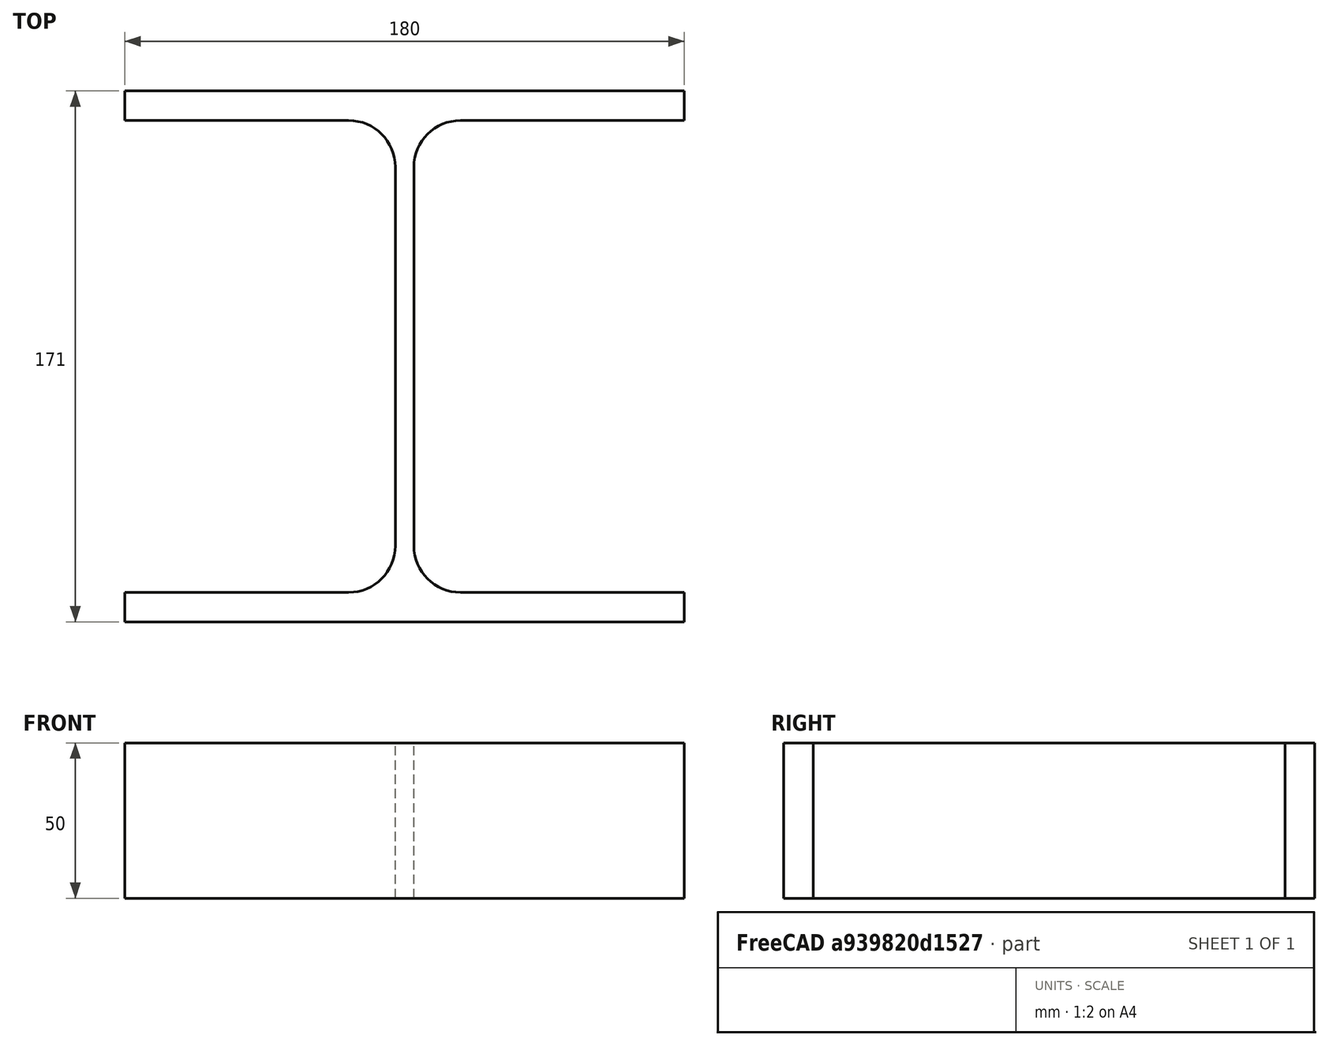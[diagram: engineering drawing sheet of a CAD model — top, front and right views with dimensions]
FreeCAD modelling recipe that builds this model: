
FCSTD DOCUMENT  (FreeCAD 0.15R4671 (Git))
Label: HE-A-Profile 180 DIN1025-3 S235JR
License: All rights reserved
LicenseURL: http://en.wikipedia.org/wiki/All_rights_reserved
objects: Sketcher::SketchObject×1, Part::Extrusion×1
note: 2 computed .brp shape members not serialized (recipe doc carries the construction recipe); baked Part::Feature solids carry a one-line shape summary decoded from their .brp

FEATURE [Sketcher::SketchObject] Sketch
  sketch-geometry (16):
    g0: LineSegment StartX=3 StartY=-61 StartZ=0 EndX=3 EndY=61 EndZ=0
    g1: LineSegment StartX=18 StartY=76 StartZ=0 EndX=90 EndY=76 EndZ=0
    g2: LineSegment StartX=90 StartY=76 StartZ=0 EndX=90 EndY=85.5 EndZ=0
    g3: LineSegment StartX=90 StartY=85.5 StartZ=0 EndX=-90 EndY=85.5 EndZ=0
    g4: LineSegment StartX=-90 StartY=85.5 StartZ=0 EndX=-90 EndY=76 EndZ=0
    g5: LineSegment StartX=-90 StartY=76 StartZ=0 EndX=-18 EndY=76 EndZ=0
    g6: LineSegment StartX=-3 StartY=61 StartZ=0 EndX=-3 EndY=-61 EndZ=0
    g7: LineSegment StartX=-18 StartY=-76 StartZ=0 EndX=-90 EndY=-76 EndZ=0
    g8: LineSegment StartX=-90 StartY=-76 StartZ=0 EndX=-90 EndY=-85.5 EndZ=0
    g9: LineSegment StartX=-90 StartY=-85.5 StartZ=0 EndX=90 EndY=-85.5 EndZ=0
    g10: LineSegment StartX=90 StartY=-85.5 StartZ=0 EndX=90 EndY=-76 EndZ=0
    g11: LineSegment StartX=90 StartY=-76 StartZ=0 EndX=18 EndY=-76 EndZ=0
    g12: ArcOfCircle CenterX=18 CenterY=61 CenterZ=0 NormalX=0 NormalY=0 NormalZ=1 Radius=15 StartAngle=1.5708 EndAngle=3.14159
    g13: ArcOfCircle CenterX=18 CenterY=-61 CenterZ=0 NormalX=0 NormalY=0 NormalZ=1 Radius=15 StartAngle=3.14159 EndAngle=4.71239
    g14: ArcOfCircle CenterX=-18 CenterY=61 CenterZ=0 NormalX=0 NormalY=0 NormalZ=1 Radius=15 StartAngle=0 EndAngle=1.5708
    g15: ArcOfCircle CenterX=-18 CenterY=-61 CenterZ=0 NormalX=0 NormalY=0 NormalZ=1 Radius=15 StartAngle=4.71239 EndAngle=6.28319
  constraints (42):
    c: Vertical(g0)
    c: Coincident(g2,g1)
    c: Vertical(g2)
    c: Coincident(g3,g2)
    c: Coincident(g4,g3)
    c: Vertical(g4)
    c: Coincident(g5,g4)
    c: Horizontal(g5)
    c: Vertical(g6)
    c: Horizontal(g7)
    c: Coincident(g8,g7)
    c: Vertical(g8)
    c: Coincident(g9,g8)
    c: Horizontal(g9)
    c: Coincident(g10,g9)
    c: Vertical(g10)
    c: Coincident(g11,g10)
    c: Horizontal(g11)
    c: Tangent(g1,g12) = 1.5708
    c: Tangent(g0,g12) = 1.5708
    c: Tangent(g0,g13) = 1.5708
    c: Tangent(g11,g13) = 1.5708
    c: Tangent(g5,g14) = 1.5708
    c: Tangent(g6,g14) = 1.5708
    c: Tangent(g6,g15) = 1.5708
    c: Tangent(g7,g15) = 1.5708
    c: Equal(g3,g9)
    c: Equal(g2,g4)
    c: Equal(g4,g8)
    c: Equal(g8,g10)
    c: Equal(g12,g14)
    c: Equal(g14,g15)
    c: Equal(g15,g13)
    c: Symmetric(g2,g3,g-2)
    c: Symmetric(g9,g8,g-2)
    c: Symmetric(g0,g6,g-2)
    c: Symmetric(g2,g9,g-1)
    c: DistanceY(g2,g9) = -171
    c: DistanceX(g3) = -180
    c: DistanceX(g0,g6) = -6
    c: DistanceY(g2) = 9.5
    c: Radius(g12) = 15
FEATURE [Part::Extrusion] Extrude  label="HE-A-Profile 180 DIN1025-3 S235JR"
  Base = -> Sketch
  Dir = (0,0,50)
  Solid = true
